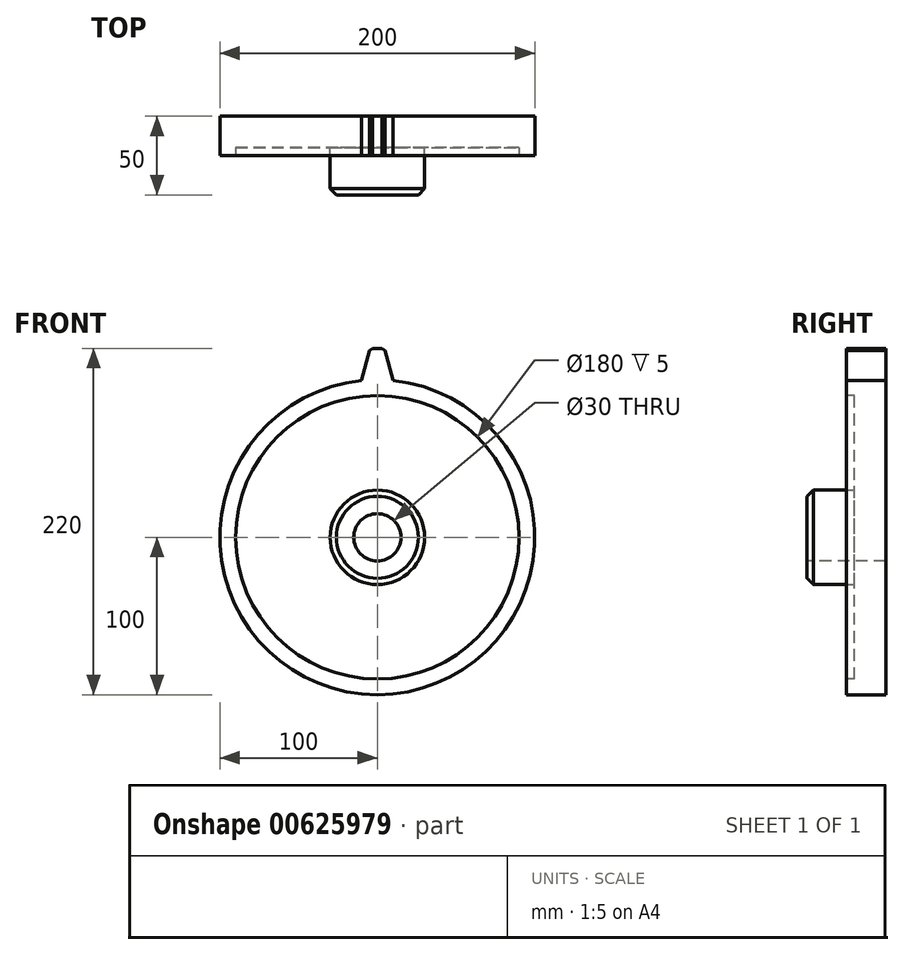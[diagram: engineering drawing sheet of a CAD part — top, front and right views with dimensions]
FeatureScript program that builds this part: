
annotation { "Feature Type Name" : "Feature", "Feature Type Description" : "" }
export const myFeature = defineFeature(function(context is Context, id is Id, definition is map)
    precondition{}
    {
        {
            var Q0;
            Q0=qCreatedBy(makeId("Front.planeOp"),FACE);
            var sketch = newSketch(context, id + "F0", { "sketchPlane" : qUnion([Q0])});
            skCircle(sketch, "E0", {"center": v(0, 0) * mm, "radius": 100 * mm});
            skSolve(sketch);
        }
        {
            var Q0;
            Q0=makeQuery(id+"F0.imprint","IMPRINT",FACE,{"disambiguationData":[TD([[makeQuery(id+"F0.imprint","IMPRINT",EDGE,{"derivedFrom":sQuery(id+"F0.wireOp",EDGE,"E0")}),1.0]])]});
            extrude(context, id + "F1", {"entities" : qUnion([Q0]), "depth" : 25 * mm, "offsetDistance" : 25 * mm});
        }
        {
            var Q0;
            Q0=makeQuery(id+"F1.opExtrude","CAP_FACE",FACE,{"disambiguationData":[OSD([sQuery(id+"F0.wireOp",EDGE,"E0")])],"isStart":false});
            var sketch = newSketch(context, id + "F2", { "sketchPlane" : qUnion([Q0])});
            skLineSegment(sketch, "E1", {"start": v(-10, 99.5) * mm, "end": v(10, 99.5) * mm});
            skLineSegment(sketch, "E2", {"start": v(10, 99.5) * mm, "end": v(4.5, 120) * mm});
            skLineSegment(sketch, "E3", {"start": v(4.5, 120) * mm, "end": v(-4.5, 120) * mm});
            skLineSegment(sketch, "E4", {"start": v(-4.5, 120) * mm, "end": v(-10, 99.5) * mm});
            skSolve(sketch);
        }
        {
            var Q0;
            {var subQ0=sQuery(id+"F2.wireOp",EDGE,"E2");Q0=makeQuery(id+"F2.imprint","IMPRINT",FACE,{"disambiguationData":[TD([[makeQuery(id+"F2.imprint","IMPRINT",EDGE,{"derivedFrom":subQ0}),1.0]])]});}
            var Q1;
            Q1=makeQuery(id+"F1.opExtrude","CAP_FACE",FACE,{"disambiguationData":[OSD([sQuery(id+"F0.wireOp",EDGE,"E0")])],"isStart":true});
            extrude(context, id + "F3", {"entities" : qUnion([Q0]), "operationType" : NewBodyOperationType.ADD, "endBound" : BoundingType.UP_TO_SURFACE, "oppositeDirection" : true, "depth" : 25 * mm, "endBoundEntityFace" : qUnion([Q1]), "offsetDistance" : 25 * mm});
        }
        {
            var Q0;
            Q0=makeQuery(id+"F3.opExtrude","SWEPT_EDGE",EDGE,{"disambiguationData":[OSD([sQuery(id+"F0.wireOp",EDGE,"E0"),sQuery(id+"F2.wireOp",EDGE,"E1"),sQuery(id+"F2.wireOp",EDGE,"E2")])]});
            var Q1;
            Q1=makeQuery(id+"F3.opExtrude","SWEPT_EDGE",EDGE,{"disambiguationData":[OSD([sQuery(id+"F0.wireOp",EDGE,"E0"),sQuery(id+"F2.wireOp",EDGE,"E1"),sQuery(id+"F2.wireOp",EDGE,"E4")])]});
            fillet(context, id + "F4", {"entities" : qUnion([Q0, Q1]), "radius" : 5 * mm, "tangentPropagation" : true, "allowEdgeOverflow" : false});
        }
        {
            var Q0;
            Q0=makeQuery(id+"F3.opExtrude","SWEPT_EDGE",EDGE,{"disambiguationData":[OSD([sQuery(id+"F2.wireOp",EDGE,"E2"),sQuery(id+"F2.wireOp",EDGE,"E3")])]});
            var Q1;
            Q1=makeQuery(id+"F3.opExtrude","SWEPT_EDGE",EDGE,{"disambiguationData":[OSD([sQuery(id+"F2.wireOp",EDGE,"E3"),sQuery(id+"F2.wireOp",EDGE,"E4")])]});
            chamfer(context, id + "F5", {"entities" : qUnion([Q0, Q1]), "width" : 2 * mm, "tangentPropagation" : true});
        }
        {
            var Q0;
            {var subQ0=sQuery(id+"F2.wireOp",EDGE,"E4");var subQ1=sQuery(id+"F2.wireOp",EDGE,"E3");var subQ2=sQuery(id+"F2.wireOp",EDGE,"E2");var subQ3=sQuery(id+"F0.wireOp",EDGE,"E0");Q0=makeQuery(id+"F8v0rt8CvXKjcq5_1.19.F3.boolean.opBoolean","MERGE",FACE,{"derivedFrom":[makeQuery(id+"F8v0rt8CvXKjcq5_1.18.F3.boolean.opBoolean","MERGE",FACE,{"derivedFrom":[makeQuery(id+"F8v0rt8CvXKjcq5_1.17.F3.boolean.opBoolean","MERGE",FACE,{"derivedFrom":[makeQuery(id+"F8v0rt8CvXKjcq5_1.16.F3.boolean.opBoolean","MERGE",FACE,{"derivedFrom":[makeQuery(id+"F8v0rt8CvXKjcq5_1.15.F3.boolean.opBoolean","MERGE",FACE,{"derivedFrom":[makeQuery(id+"F8v0rt8CvXKjcq5_1.14.F3.boolean.opBoolean","MERGE",FACE,{"derivedFrom":[makeQuery(id+"F8v0rt8CvXKjcq5_1.13.F3.boolean.opBoolean","MERGE",FACE,{"derivedFrom":[makeQuery(id+"F8v0rt8CvXKjcq5_1.12.F3.boolean.opBoolean","MERGE",FACE,{"derivedFrom":[makeQuery(id+"F8v0rt8CvXKjcq5_1.11.F3.boolean.opBoolean","MERGE",FACE,{"derivedFrom":[makeQuery(id+"F8v0rt8CvXKjcq5_1.10.F3.boolean.opBoolean","MERGE",FACE,{"derivedFrom":[makeQuery(id+"F8v0rt8CvXKjcq5_1.9.F3.boolean.opBoolean","MERGE",FACE,{"derivedFrom":[makeQuery(id+"F8v0rt8CvXKjcq5_1.8.F3.boolean.opBoolean","MERGE",FACE,{"derivedFrom":[makeQuery(id+"F8v0rt8CvXKjcq5_1.7.F3.boolean.opBoolean","MERGE",FACE,{"derivedFrom":[makeQuery(id+"F8v0rt8CvXKjcq5_1.6.F3.boolean.opBoolean","MERGE",FACE,{"derivedFrom":[makeQuery(id+"F8v0rt8CvXKjcq5_1.5.F3.boolean.opBoolean","MERGE",FACE,{"derivedFrom":[makeQuery(id+"F8v0rt8CvXKjcq5_1.4.F3.boolean.opBoolean","MERGE",FACE,{"derivedFrom":[makeQuery(id+"F8v0rt8CvXKjcq5_1.3.F3.boolean.opBoolean","MERGE",FACE,{"derivedFrom":[makeQuery(id+"F8v0rt8CvXKjcq5_1.2.F3.boolean.opBoolean","MERGE",FACE,{"derivedFrom":[makeQuery(id+"F8v0rt8CvXKjcq5_1.1.F3.boolean.opBoolean","MERGE",FACE,{"derivedFrom":[makeQuery(id+"F3.boolean.opBoolean","MERGE",FACE,{"derivedFrom":[makeQuery(id+"F1.opExtrude","CAP_FACE",FACE,{"disambiguationData":[OSD([subQ3])],"isStart":false}),makeQuery(id+"F3.opExtrude","CAP_FACE",FACE,{"disambiguationData":[OSD([subQ3,subQ2,subQ1,subQ0])],"isStart":true})]}),makeQuery(id+"F8v0rt8CvXKjcq5_1.1.F3.opExtrude","CAP_FACE",FACE,{"disambiguationData":[OSD([subQ3,subQ2,subQ1,subQ0])],"isStart":true})]}),makeQuery(id+"F8v0rt8CvXKjcq5_1.2.F3.opExtrude","CAP_FACE",FACE,{"disambiguationData":[OSD([subQ3,subQ2,subQ1,subQ0])],"isStart":true})]}),makeQuery(id+"F8v0rt8CvXKjcq5_1.3.F3.opExtrude","CAP_FACE",FACE,{"disambiguationData":[OSD([subQ3,subQ2,subQ1,subQ0])],"isStart":true})]}),makeQuery(id+"F8v0rt8CvXKjcq5_1.4.F3.opExtrude","CAP_FACE",FACE,{"disambiguationData":[OSD([subQ3,subQ2,subQ1,subQ0])],"isStart":true})]}),makeQuery(id+"F8v0rt8CvXKjcq5_1.5.F3.opExtrude","CAP_FACE",FACE,{"disambiguationData":[OSD([subQ3,subQ2,subQ1,subQ0])],"isStart":true})]}),makeQuery(id+"F8v0rt8CvXKjcq5_1.6.F3.opExtrude","CAP_FACE",FACE,{"disambiguationData":[OSD([subQ3,subQ2,subQ1,subQ0])],"isStart":true})]}),makeQuery(id+"F8v0rt8CvXKjcq5_1.7.F3.opExtrude","CAP_FACE",FACE,{"disambiguationData":[OSD([subQ3,subQ2,subQ1,subQ0])],"isStart":true})]}),makeQuery(id+"F8v0rt8CvXKjcq5_1.8.F3.opExtrude","CAP_FACE",FACE,{"disambiguationData":[OSD([subQ3,subQ2,subQ1,subQ0])],"isStart":true})]}),makeQuery(id+"F8v0rt8CvXKjcq5_1.9.F3.opExtrude","CAP_FACE",FACE,{"disambiguationData":[OSD([subQ3,subQ2,subQ1,subQ0])],"isStart":true})]}),makeQuery(id+"F8v0rt8CvXKjcq5_1.10.F3.opExtrude","CAP_FACE",FACE,{"disambiguationData":[OSD([subQ3,subQ2,subQ1,subQ0])],"isStart":true})]}),makeQuery(id+"F8v0rt8CvXKjcq5_1.11.F3.opExtrude","CAP_FACE",FACE,{"disambiguationData":[OSD([subQ3,subQ2,subQ1,subQ0])],"isStart":true})]}),makeQuery(id+"F8v0rt8CvXKjcq5_1.12.F3.opExtrude","CAP_FACE",FACE,{"disambiguationData":[OSD([subQ3,subQ2,subQ1,subQ0])],"isStart":true})]}),makeQuery(id+"F8v0rt8CvXKjcq5_1.13.F3.opExtrude","CAP_FACE",FACE,{"disambiguationData":[OSD([subQ3,subQ2,subQ1,subQ0])],"isStart":true})]}),makeQuery(id+"F8v0rt8CvXKjcq5_1.14.F3.opExtrude","CAP_FACE",FACE,{"disambiguationData":[OSD([subQ3,subQ2,subQ1,subQ0])],"isStart":true})]}),makeQuery(id+"F8v0rt8CvXKjcq5_1.15.F3.opExtrude","CAP_FACE",FACE,{"disambiguationData":[OSD([subQ3,subQ2,subQ1,subQ0])],"isStart":true})]}),makeQuery(id+"F8v0rt8CvXKjcq5_1.16.F3.opExtrude","CAP_FACE",FACE,{"disambiguationData":[OSD([subQ3,subQ2,subQ1,subQ0])],"isStart":true})]}),makeQuery(id+"F8v0rt8CvXKjcq5_1.17.F3.opExtrude","CAP_FACE",FACE,{"disambiguationData":[OSD([subQ3,subQ2,subQ1,subQ0])],"isStart":true})]}),makeQuery(id+"F8v0rt8CvXKjcq5_1.18.F3.opExtrude","CAP_FACE",FACE,{"disambiguationData":[OSD([subQ3,subQ2,subQ1,subQ0])],"isStart":true})]}),makeQuery(id+"F8v0rt8CvXKjcq5_1.19.F3.opExtrude","CAP_FACE",FACE,{"disambiguationData":[OSD([subQ3,subQ2,subQ1,subQ0])],"isStart":true})]});}
            var sketch = newSketch(context, id + "F6", { "sketchPlane" : qUnion([Q0])});
            skCircle(sketch, "E5", {"center": v(0, 0) * mm, "radius": 90 * mm});
            skSolve(sketch);
        }
        {
            var Q0;
            Q0 = qSketchRegion(id + "F6", true);
            extrude(context, id + "F7", {"entities" : qUnion([Q0]), "operationType" : NewBodyOperationType.REMOVE, "oppositeDirection" : true, "depth" : 5 * mm, "offsetDistance" : 25 * mm});
        }
        {
            var Q0;
            Q0=makeQuery(id+"F7.boolean.opBoolean","COPY",FACE,{"derivedFrom":makeQuery(id+"F7.opExtrude","CAP_FACE",FACE,{"disambiguationData":[OSD([sQuery(id+"F6.wireOp",EDGE,"E5")])],"isStart":false})});
            var sketch = newSketch(context, id + "F8", { "sketchPlane" : qUnion([Q0])});
            skCircle(sketch, "E6", {"center": v(0, 0) * mm, "radius": 30 * mm});
            skSolve(sketch);
        }
        {
            var Q0;
            Q0 = qSketchRegion(id + "F8", true);
            extrude(context, id + "F9", {"entities" : qUnion([Q0]), "operationType" : NewBodyOperationType.ADD, "depth" : 30 * mm, "offsetDistance" : 25 * mm});
        }
        {
            var Q0;
            Q0=makeQuery(id+"F9.opExtrude","CAP_FACE",FACE,{"disambiguationData":[OSD([sQuery(id+"F8.wireOp",EDGE,"E6")])],"isStart":false});
            var sketch = newSketch(context, id + "F10", { "sketchPlane" : qUnion([Q0])});
            skCircle(sketch, "E7", {"center": v(0, 0) * mm, "radius": 15 * mm});
            skSolve(sketch);
        }
        {
            var Q0;
            Q0 = qSketchRegion(id + "F10", true);
            extrude(context, id + "F11", {"entities" : qUnion([Q0]), "operationType" : NewBodyOperationType.REMOVE, "endBound" : BoundingType.THROUGH_ALL, "oppositeDirection" : true, "depth" : 25 * mm, "offsetDistance" : 25 * mm});
        }
        {
            var Q0;
            Q0=makeQuery(id+"F9.opExtrude","CAP_EDGE",EDGE,{"disambiguationData":[OSD([sQuery(id+"F8.wireOp",EDGE,"E6")])],"isStart":false});
            var Q1;
            Q1=makeQuery(id+"F11.boolean.opBoolean","COPY",EDGE,{"derivedFrom":makeQuery(id+"F11.opExtrude","CAP_EDGE",EDGE,{"disambiguationData":[OSD([sQuery(id+"F10.wireOp",EDGE,"E7")])],"isStart":true})});
            chamfer(context, id + "F12", {"entities" : qUnion([Q0, Q1]), "width" : 4 * mm, "tangentPropagation" : true});
        }
    });
